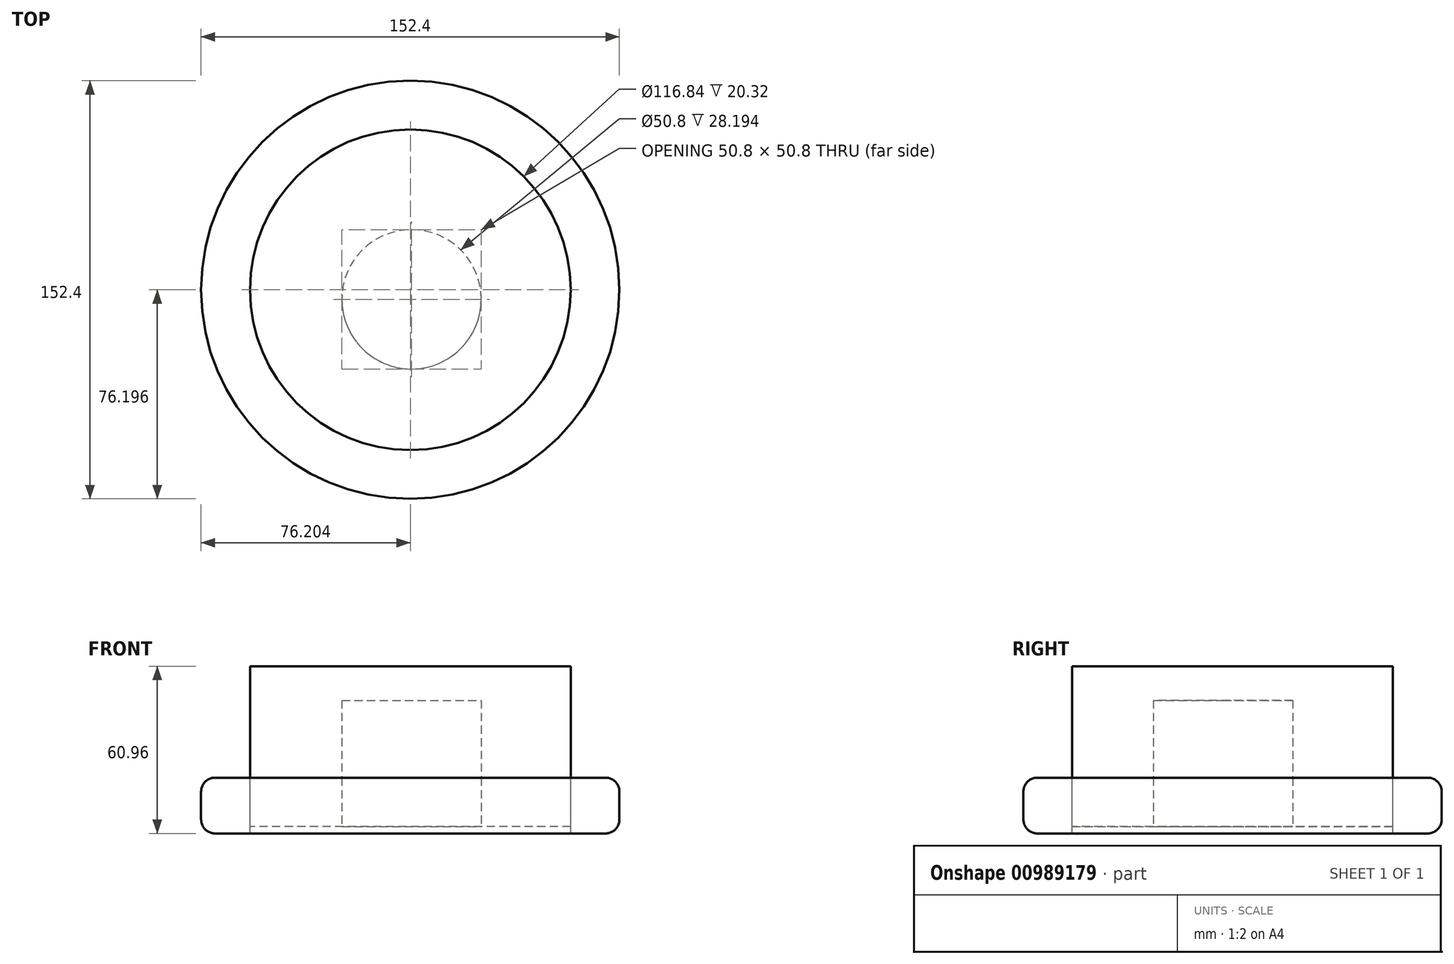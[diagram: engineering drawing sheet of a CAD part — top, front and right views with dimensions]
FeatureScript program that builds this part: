
annotation { "Feature Type Name" : "Feature", "Feature Type Description" : "" }
export const myFeature = defineFeature(function(context is Context, id is Id, definition is map)
    precondition{}
    {
        {
            var Q0;
            Q0=qCreatedBy(makeId("Top.planeOp"),FACE);
            var sketch = newSketch(context, id + "F0", { "sketchPlane" : qUnion([Q0])});
            skCircle(sketch, "E0", {"center": v(-23.13, 3.47) * mm, "radius": 58.42 * mm});
            skSolve(sketch);
        }
        {
            var Q0;
            Q0=makeQuery(id+"F0.imprint","IMPRINT",FACE,{"disambiguationData":[TD([[makeQuery(id+"F0.imprint","IMPRINT",EDGE,{"derivedFrom":sQuery(id+"F0.wireOp",EDGE,"E0")}),1.0]])]});
            extrude(context, id + "F1", {"entities" : qUnion([Q0]), "depth" : 40.64 * mm, "offsetDistance" : 25.4 * mm});
        }
        {
            var Q0;
            Q0=makeQuery(id+"F1.opExtrude","CAP_FACE",FACE,{"disambiguationData":[OSD([sQuery(id+"F0.wireOp",EDGE,"E0")])],"isStart":true});
            var sketch = newSketch(context, id + "F2", { "sketchPlane" : qUnion([Q0])});
            skCircle(sketch, "E1", {"center": v(-23.13, -3.47) * mm, "radius": 76.2 * mm});
            skSolve(sketch);
        }
        {
            var Q0;
            Q0=makeQuery(id+"F2.imprint","IMPRINT",FACE,{"disambiguationData":[TD([[makeQuery(id+"F2.imprint","IMPRINT",EDGE,{"derivedFrom":sQuery(id+"F2.wireOp",EDGE,"E1")}),1.0]])]});
            extrude(context, id + "F3", {"entities" : qUnion([Q0]), "depth" : 20.32 * mm, "offsetDistance" : 25.4 * mm});
        }
        {
            var Q0;
            Q0=makeQuery(id+"F3.opExtrude","SWEPT_FACE",FACE,{"disambiguationData":[OSD([sQuery(id+"F2.wireOp",EDGE,"E1")])]});
            fillet(context, id + "F4", {"entities" : qUnion([Q0]), "radius" : 5.08 * mm, "tangentPropagation" : true, "allowEdgeOverflow" : false});
        }
        {
            var Q0;
            Q0=makeQuery(id+"F1.opExtrude","CAP_FACE",FACE,{"disambiguationData":[OSD([sQuery(id+"F0.wireOp",EDGE,"E0")])],"isStart":true});
            extrude(context, id + "F5", {"entities" : qUnion([Q0]), "depth" : 17.78 * mm, "offsetDistance" : 25.4 * mm});
        }
        {
            var Q0;
            Q0=makeQuery(id+"F5.opExtrude","CAP_FACE",FACE,{"disambiguationData":[OSD([sQuery(id+"F0.wireOp",EDGE,"E0")])],"isStart":false});
            var sketch = newSketch(context, id + "F6", { "sketchPlane" : qUnion([Q0])});
            skSolve(sketch);
        }
        {
            var Q0;
            Q0=makeQuery(id+"F6.imprint","IMPRINT",FACE,{"disambiguationData":[TD([[makeQuery(id+"F6.imprint","IMPRINT",EDGE,{"derivedFrom":makeQuery(id+"F5.opExtrude","CAP_EDGE",EDGE,{"disambiguationData":[OSD([sQuery(id+"F0.wireOp",EDGE,"E0")])],"isStart":false})}),-1.0]])]});
            var sketch = newSketch(context, id + "F7", { "sketchPlane" : qUnion([Q0])});
            skCircle(sketch, "E2", {"center": v(-22.67, 0) * mm, "radius": 25.4 * mm});
            skSolve(sketch);
        }
        {
            var Q0;
            Q0=makeQuery(id+"F7.imprint","IMPRINT",FACE,{"disambiguationData":[TD([[makeQuery(id+"F7.imprint","IMPRINT",EDGE,{"derivedFrom":sQuery(id+"F7.wireOp",EDGE,"E2")}),1.0]])]});
            extrude(context, id + "F8", {"entities" : qUnion([Q0]), "operationType" : NewBodyOperationType.REMOVE, "oppositeDirection" : true, "depth" : 45.97 * mm, "offsetDistance" : 25.4 * mm});
        }
    });
